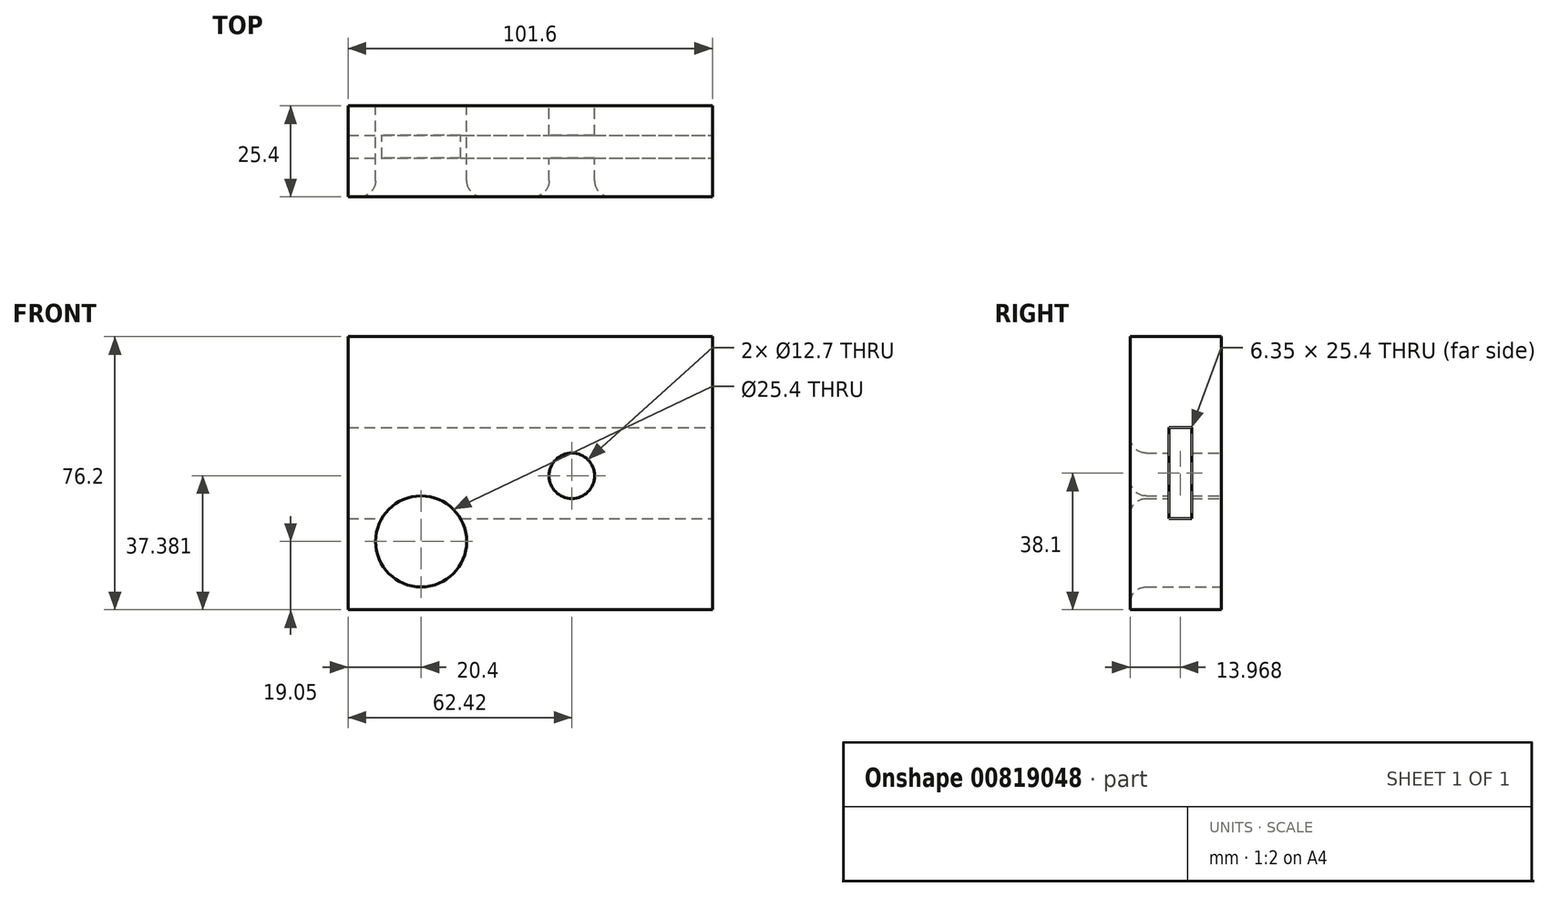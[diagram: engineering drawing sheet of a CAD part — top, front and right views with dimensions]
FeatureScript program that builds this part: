
annotation { "Feature Type Name" : "Feature", "Feature Type Description" : "" }
export const myFeature = defineFeature(function(context is Context, id is Id, definition is map)
    precondition{}
    {
        {
            var Q0;
            Q0=qCreatedBy(makeId("Front.planeOp"),FACE);
            var sketch = newSketch(context, id + "F0", { "sketchPlane" : qUnion([Q0])});
            skLineSegment(sketch, "E0.bottom", {"start": v(-45.8, -19.05) * mm, "end": v(55.8, -19.05) * mm});
            skLineSegment(sketch, "E0.top", {"start": v(-45.8, 57.15) * mm, "end": v(55.8, 57.15) * mm});
            skLineSegment(sketch, "E0.left", {"start": v(-45.8, -19.05) * mm, "end": v(-45.8, 57.15) * mm});
            skLineSegment(sketch, "E0.right", {"start": v(55.8, -19.05) * mm, "end": v(55.8, 57.15) * mm});
            skCircle(sketch, "E1", {"center": v(16.62, 18.33) * mm, "radius": 6.35 * mm});
            skCircle(sketch, "E2", {"center": v(-25.4, 0) * mm, "radius": 12.7 * mm});
            skSolve(sketch);
        }
        {
            var Q0;
            Q0=makeQuery(id+"F0.imprint","IMPRINT",FACE,{"disambiguationData":[TD([[makeQuery(id+"F0.imprint","IMPRINT",EDGE,{"derivedFrom":sQuery(id+"F0.wireOp",EDGE,"E0.bottom")}),1.0]])]});
            extrude(context, id + "F1", {"entities" : qUnion([Q0]), "depth" : 25.4 * mm, "offsetDistance" : 25.4 * mm});
        }
        {
            var Q0;
            Q0=makeQuery(id+"F1.opExtrude","CAP_EDGE",EDGE,{"disambiguationData":[OSD([sQuery(id+"F0.wireOp",EDGE,"E2")])],"isStart":false});
            var Q1;
            Q1=makeQuery(id+"F1.opExtrude","CAP_EDGE",EDGE,{"disambiguationData":[OSD([sQuery(id+"F0.wireOp",EDGE,"E1")])],"isStart":false});
            fillet(context, id + "F2", {"entities" : qUnion([Q0, Q1]), "radius" : 4.44 * mm, "tangentPropagation" : true, "allowEdgeOverflow" : false});
        }
        {
            var Q0;
            Q0=makeQuery(id+"F1.opExtrude","SWEPT_FACE",FACE,{"disambiguationData":[OSD([sQuery(id+"F0.wireOp",EDGE,"E0.right")])]});
            var sketch = newSketch(context, id + "F3", { "sketchPlane" : qUnion([Q0])});
            skLineSegment(sketch, "E3.bottom", {"start": v(-8.26, 31.75) * mm, "end": v(-14.6, 31.75) * mm});
            skLineSegment(sketch, "E3.top", {"start": v(-8.26, 6.35) * mm, "end": v(-14.6, 6.35) * mm});
            skLineSegment(sketch, "E3.left", {"start": v(-8.26, 31.75) * mm, "end": v(-8.26, 6.35) * mm});
            skLineSegment(sketch, "E3.right", {"start": v(-14.6, 31.75) * mm, "end": v(-14.6, 6.35) * mm});
            skPoint(sketch, "E3.middle", {"position": v(-11.43, 19.05) * mm});
            skSolve(sketch);
        }
        {
            var Q0;
            Q0=makeQuery(id+"F3.imprint","IMPRINT",FACE,{"disambiguationData":[TD([[makeQuery(id+"F3.imprint","IMPRINT",EDGE,{"derivedFrom":sQuery(id+"F3.wireOp",EDGE,"E3.bottom")}),1.0]])]});
            extrude(context, id + "F4", {"entities" : qUnion([Q0]), "operationType" : NewBodyOperationType.REMOVE, "endBound" : BoundingType.THROUGH_ALL, "oppositeDirection" : true, "depth" : 25.4 * mm, "offsetDistance" : 25.4 * mm});
        }
    });
